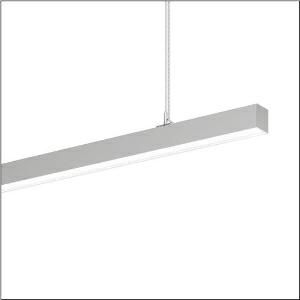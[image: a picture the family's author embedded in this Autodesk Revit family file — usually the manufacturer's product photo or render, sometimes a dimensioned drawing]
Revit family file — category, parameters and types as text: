
# Revit family: silica_r__21_51mx30tat4s_875d
name_source: partatom
category: Lighting Fixtures
units: mm (PartAtom-declared; Revit-internal decimal feet)

## family parameters
Cut with Voids When Loaded = No
Host = Face
Light Source = No
Part Type = Normal
Room Calculation Point = No
Round Connector Dimension = Use Diameter
Shared = No

## types (1)
- --- (1 x LED, 4120 lm, 33.8 W, 6500K)
    Apparent Load = 34 VA
    CIE Flux Codes = 47 79 96 58 100
    Color Rendering = 80
    Color Temperature = 6500K
    Default Elevation = 1800 mm
    Description = Silica® 21, office luminaire, primary optical cover: cover, of PMMA, opal, light emission: direct/indirect distribution, primary light characteristic: symmetric, installation type: suspended mounting, LED, rated luminous flux: 4.120lm, luminous efficacy: 116lm/W, light colour: 8tw, colour temperature: 2700..6500K, control gear: ECG DALI, with terminal, 3+2-pole, max. 2.5mm², mains connection: 220..240V, AC, 50/60Hz, rated input power: 35.5W, luminaire housing, of aluminium, metallic grey (RAL 9006), length: 1.204mm, width: 53mm, height: 53mm, protection rating (complete): IP20, insulation class (complete): insulation class I (protective earthing), certification: CE, permissible operating ambient temperature: 0..+35°C, standard: EN 50419, packaging unit: 1 piece
    Height = 53 mm
    Lamp = 1 x LED
    Lamp Light Flux = 4120 lm
    Lamp Power = 33.8 W
    Lamp count = 1
    Length = 1204 mm
    Luminous efficacy = 122 lm/W
    Manufacturer = Siteco
    ModVariant = No
    Model = 51MX30TAT4S
    Mounting Place = Ceiling
    Mounting Type = Pendant
    Number of Poles = 1
    OnlyDefault = Yes
    Power Factor = 1
    Product Name = Silica® 21
    Product group = office luminaire | ceiling pendant
    ProductGroupID = 902
    Protection Class = Protection class I
    Protection Degree = IP 20
    RLX_Detail_Level = 1
    RLX_Emergency_Light_Flux = 0 lm
    RLX_Emergency_Type = 0
    RLX_Emergency_Type_DB = No
    RlxData = <blob elided: 20145 chars, md5=2de764b2>
    Socket = socket
    Standby Power = 0 W
    System Light Flux = 4120 lm
    System Power = 34 W
    Type Comments = individual setting
    Type Image = l_1297747.jpg
    URL = http://relux.com
    VarID = @adj_070945
    Voltage = 0 V
    Weight = 0.00 kg
    Width = 53 mm

## geometry (parser evidence)
native form markers: Blend x4, Sweep x11
no freeform markers — native parametric forms only
